AUTODESK INVENTOR PART (.ipt)
format: ipt  version: 2014 (Build 180170000, 170)  size: 120,320 bytes
history: native  units: mm
features: extrude x4, sketch x4, fillet x2
ambient origin geometry x8: Origin, YZ Plane, XZ Plane, XY Plane, X Axis, Y Axis, Z Axis, Center Point
bodies: Solid1 (feature_tree)
feature tree (10):
  extrude  "Extrusion1"  Depth=70.0mm
  extrude  "Extrusion2"  Depth=65.2mm
  extrude  "Extrusion3"  Depth=40.0mm TaperAngle=0.0deg
  extrude  "Extrusion4"  Depth=2.3mm TaperAngle=0.0deg
  fillet  "Fillet1"  Radius=10.0mm
  fillet  "Fillet2"  Radius=4.0mm
  sketch  "Sketch1"  dims[d0=70.0mm d1=100.0mm]
  sketch  "Sketch2"  dims[d2=2.4mm d3=0.0mm d4=65.2mm]
  sketch  "Sketch3"  dims[d5=95.2mm d6=40.0mm d7=0.0mm]
  sketch  "Sketch4"  dims[d8=40.0mm d9=0.0mm d10=2.3mm d11=0.0mm d12=10.0mm d13=4.0mm]
